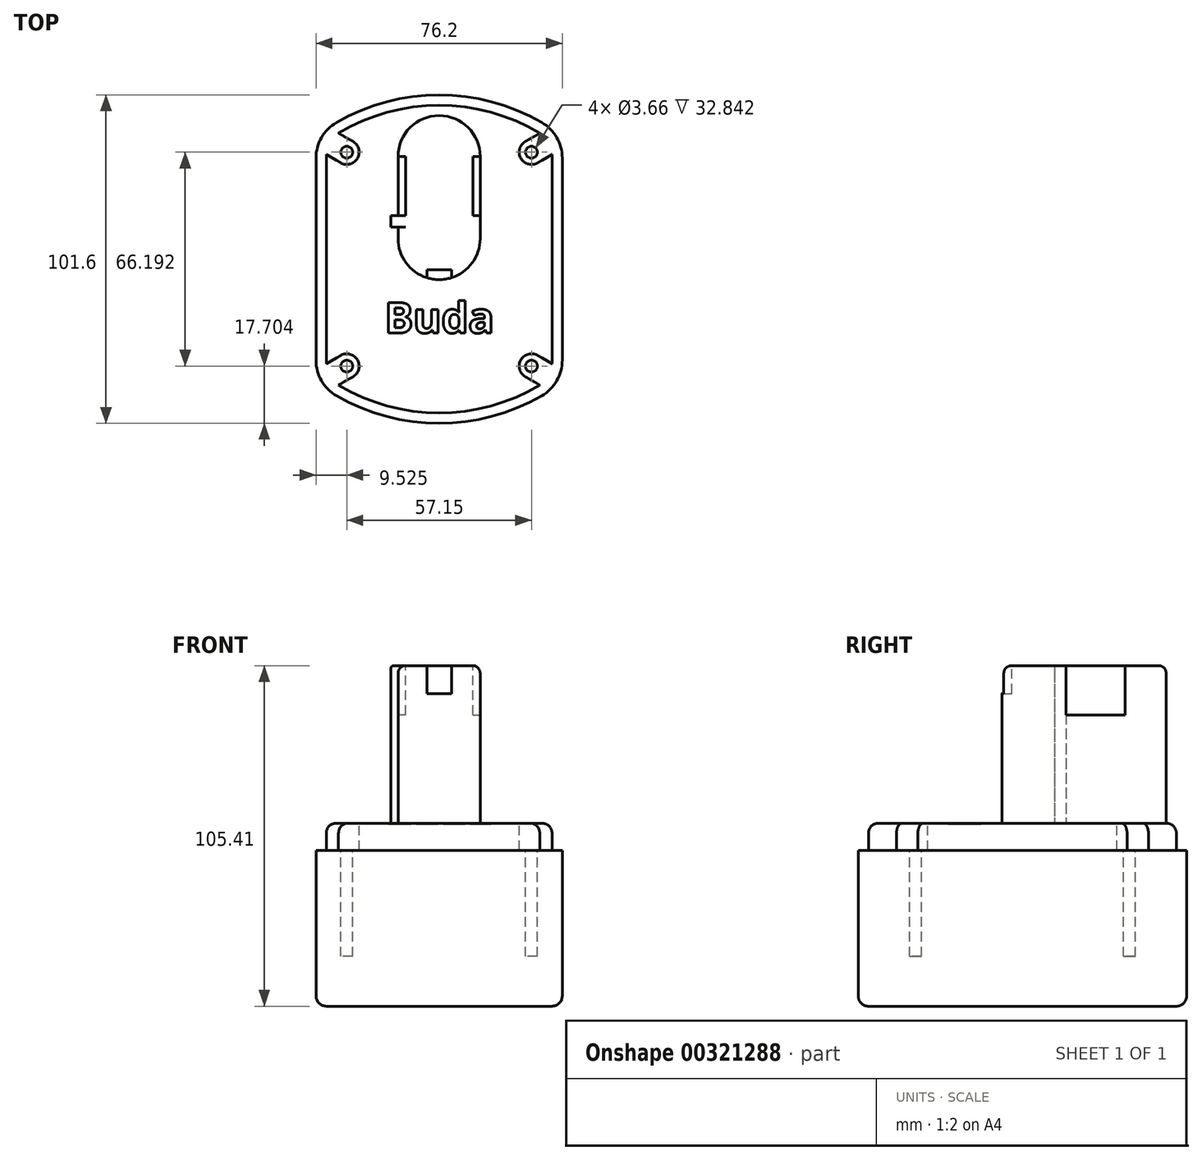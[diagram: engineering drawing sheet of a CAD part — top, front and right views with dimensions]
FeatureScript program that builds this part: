
annotation { "Feature Type Name" : "Feature", "Feature Type Description" : "" }
export const myFeature = defineFeature(function(context is Context, id is Id, definition is map)
    precondition{}
    {
        {
            var Q0;
            Q0=qCreatedBy(makeId("Top.planeOp"),FACE);
            var sketch = newSketch(context, id + "F0", { "sketchPlane" : qUnion([Q0])});
            skLineSegment(sketch, "E0.bottom", {"start": v(38.1, 38.1) * mm, "end": v(-38.1, 38.1) * mm, "construction": true});
            skLineSegment(sketch, "E0.top", {"start": v(38.1, -38.1) * mm, "end": v(-38.1, -38.1) * mm, "construction": true});
            skLineSegment(sketch, "E0.left", {"start": v(38.1, 38.1) * mm, "end": v(38.1, -38.1) * mm});
            skLineSegment(sketch, "E0.right", {"start": v(-38.1, 38.1) * mm, "end": v(-38.1, -38.1) * mm});
            skPoint(sketch, "E0.middle", {"position": v(0, 0) * mm});
            skLineSegment(sketch, "E1", {"start": v(0, 38.1) * mm, "end": v(0, 50.8) * mm, "construction": true});
            skPoint(sketch, "E1.endSnap0", {"position": v(0, 38.1) * mm});
            skArc(sketch, "E2", {"start": v(38.1, 38.1) * mm, "mid": v(0, 50.8) * mm, "end": v(-38.1, 38.1) * mm});
            skLineSegment(sketch, "E3", {"start": v(-38.1, 0) * mm, "end": v(38.1, 0) * mm, "construction": true});
            skArc(sketch, "E4.MirrorCS", {"start": v(38.1, -38.1) * mm, "mid": v(0, -50.8) * mm, "end": v(-38.1, -38.1) * mm});
            skSolve(sketch);
        }
        {
            var Q0;
            Q0 = qSketchRegion(id + "F0", true);
            extrude(context, id + "F1", {"entities" : qUnion([Q0]), "oppositeDirection" : true, "depth" : 48.26 * mm});
        }
        {
            var Q0;
            Q0=makeQuery(id+"F1.opExtrude","CAP_FACE",FACE,{"disambiguationData":[OSD([sQuery(id+"F0.wireOp",EDGE,"E0.left"),sQuery(id+"F0.wireOp",EDGE,"E0.right"),sQuery(id+"F0.wireOp",EDGE,"E2"),sQuery(id+"F0.wireOp",EDGE,"E4.MirrorCS")])],"isStart":true});
            var sketch = newSketch(context, id + "F2", { "sketchPlane" : qUnion([Q0])});
            skArc(sketch, "E5.0.0", {"start": v(38.1, 38.1) * mm, "mid": v(0, 50.8) * mm, "end": v(-38.1, 38.1) * mm, "construction": true});
            skLineSegment(sketch, "E5.0.1", {"start": v(-38.1, 38.1) * mm, "end": v(-38.1, -38.1) * mm, "construction": true});
            skArc(sketch, "E5.0.2", {"start": v(-38.1, -38.1) * mm, "mid": v(0, -50.8) * mm, "end": v(38.1, -38.1) * mm, "construction": true});
            skLineSegment(sketch, "E5.0.3", {"start": v(38.1, -38.1) * mm, "end": v(38.1, 38.1) * mm, "construction": true});
            skArc(sketch, "E6.0", {"start": v(34.93, 36.49) * mm, "mid": v(0, 47.62) * mm, "end": v(-34.92, 36.49) * mm});
            skLineSegment(sketch, "E6.1", {"start": v(34.93, -36.49) * mm, "end": v(34.93, 36.49) * mm});
            skArc(sketch, "E6.2", {"start": v(-34.93, -36.49) * mm, "mid": v(0, -47.62) * mm, "end": v(34.93, -36.49) * mm});
            skLineSegment(sketch, "E6.3", {"start": v(-34.93, 36.49) * mm, "end": v(-34.93, -36.49) * mm});
            skSolve(sketch);
        }
        {
            var Q0;
            Q0 = qSketchRegion(id + "F2", true);
            extrude(context, id + "F3", {"entities" : qUnion([Q0]), "operationType" : NewBodyOperationType.ADD, "depth" : 8.38 * mm});
        }
        {
            var Q0;
            Q0=makeQuery(id+"F3.opExtrude","CAP_FACE",FACE,{"disambiguationData":[OSD([sQuery(id+"F2.wireOp",EDGE,"E6.0"),sQuery(id+"F2.wireOp",EDGE,"E6.1"),sQuery(id+"F2.wireOp",EDGE,"E6.2"),sQuery(id+"F2.wireOp",EDGE,"E6.3")])],"isStart":false});
            var sketch = newSketch(context, id + "F4", { "sketchPlane" : qUnion([Q0])});
            skLineSegment(sketch, "E7.bottom", {"start": v(28.58, 33.1) * mm, "end": v(-28.57, 33.1) * mm, "construction": true});
            skLineSegment(sketch, "E7.top", {"start": v(28.57, -33.1) * mm, "end": v(-28.58, -33.1) * mm, "construction": true});
            skLineSegment(sketch, "E7.left", {"start": v(28.58, 33.1) * mm, "end": v(28.57, -33.1) * mm, "construction": true});
            skLineSegment(sketch, "E7.right", {"start": v(-28.57, 33.1) * mm, "end": v(-28.58, -33.1) * mm, "construction": true});
            skPoint(sketch, "E7.middle", {"position": v(0, 0) * mm});
            skLineSegment(sketch, "E8", {"start": v(-28.58, -33.1) * mm, "end": v(-50.57, -45.8) * mm, "construction": true});
            skArc(sketch, "E9.0.startCap", {"start": v(-30.48, -29.8) * mm, "mid": v(-25.28, -31.2) * mm, "end": v(-26.67, -36.4) * mm});
            skArc(sketch, "E9.0.endCap", {"start": v(-48.67, -49.1) * mm, "mid": v(-53.87, -47.7) * mm, "end": v(-52.48, -42.5) * mm});
            skLineSegment(sketch, "E9.0.left", {"start": v(-26.67, -36.4) * mm, "end": v(-48.67, -49.1) * mm});
            skLineSegment(sketch, "E9.0.right", {"start": v(-30.48, -29.8) * mm, "end": v(-52.48, -42.5) * mm});
            skLineSegment(sketch, "E10", {"start": v(-28.58, 0) * mm, "end": v(28.58, 0) * mm, "construction": true});
            skLineSegment(sketch, "E11", {"start": v(0, 33.1) * mm, "end": v(0, -33.1) * mm, "construction": true});
            skArc(sketch, "E12.MirrorCS", {"start": v(30.48, -29.8) * mm, "mid": v(25.28, -31.2) * mm, "end": v(26.67, -36.4) * mm});
            skLineSegment(sketch, "E13.MirrorCS", {"start": v(30.48, -29.8) * mm, "end": v(52.48, -42.5) * mm});
            skLineSegment(sketch, "E14.MirrorCS", {"start": v(26.67, -36.4) * mm, "end": v(48.67, -49.1) * mm});
            skArc(sketch, "E15.MirrorCS", {"start": v(48.67, -49.1) * mm, "mid": v(53.87, -47.7) * mm, "end": v(52.48, -42.5) * mm});
            skArc(sketch, "E16.MirrorCS", {"start": v(-30.48, 29.8) * mm, "mid": v(-25.28, 31.2) * mm, "end": v(-26.67, 36.4) * mm});
            skLineSegment(sketch, "E17.MirrorCS", {"start": v(-30.48, 29.8) * mm, "end": v(-52.48, 42.5) * mm});
            skLineSegment(sketch, "E18.MirrorCS", {"start": v(-26.67, 36.4) * mm, "end": v(-48.67, 49.1) * mm});
            skArc(sketch, "E19.MirrorCS", {"start": v(-48.67, 49.1) * mm, "mid": v(-53.87, 47.7) * mm, "end": v(-52.48, 42.5) * mm});
            skArc(sketch, "E20.MirrorCS", {"start": v(30.48, 29.8) * mm, "mid": v(25.28, 31.2) * mm, "end": v(26.67, 36.4) * mm});
            skLineSegment(sketch, "E21.MirrorCS", {"start": v(30.48, 29.8) * mm, "end": v(52.48, 42.5) * mm});
            skLineSegment(sketch, "E22.MirrorCS", {"start": v(26.67, 36.4) * mm, "end": v(48.67, 49.1) * mm});
            skArc(sketch, "E23.MirrorCS", {"start": v(48.67, 49.1) * mm, "mid": v(53.87, 47.7) * mm, "end": v(52.48, 42.5) * mm});
            skCircle(sketch, "E24", {"center": v(-28.57, 33.1) * mm, "radius": 1.83 * mm, "construction": true});
            skCircle(sketch, "E25", {"center": v(28.58, 33.1) * mm, "radius": 1.83 * mm, "construction": true});
            skCircle(sketch, "E26", {"center": v(-28.58, -33.1) * mm, "radius": 1.83 * mm, "construction": true});
            skCircle(sketch, "E27", {"center": v(28.57, -33.1) * mm, "radius": 1.83 * mm, "construction": true});
            skSolve(sketch);
        }
        {
            var Q0;
            Q0 = qSketchRegion(id + "F4", true);
            var Q1;
            Q1=makeQuery(id+"F1.opExtrude","CAP_FACE",FACE,{"disambiguationData":[OSD([sQuery(id+"F0.wireOp",EDGE,"E0.left"),sQuery(id+"F0.wireOp",EDGE,"E0.right"),sQuery(id+"F0.wireOp",EDGE,"E2"),sQuery(id+"F0.wireOp",EDGE,"E4.MirrorCS")])],"isStart":true});
            extrude(context, id + "F5", {"entities" : qUnion([Q0]), "operationType" : NewBodyOperationType.REMOVE, "endBound" : BoundingType.UP_TO_SURFACE, "oppositeDirection" : true, "endBoundEntityFace" : qUnion([Q1]), "depth" : 25.4 * mm});
        }
        {
            var Q0;
            Q0=makeQuery(id+"F5.boolean.opBoolean","MERGE",FACE,{"derivedFrom":[makeQuery(id+"F1.opExtrude","CAP_FACE",FACE,{"disambiguationData":[OSD([sQuery(id+"F0.wireOp",EDGE,"E0.left"),sQuery(id+"F0.wireOp",EDGE,"E0.right"),sQuery(id+"F0.wireOp",EDGE,"E2"),sQuery(id+"F0.wireOp",EDGE,"E4.MirrorCS")])],"isStart":true})],"fromTools":[makeQuery(id+"F5.opExtrude","CAP_FACE",FACE,{"disambiguationData":[OSD([sQuery(id+"F4.wireOp",EDGE,"E9.0.startCap"),sQuery(id+"F4.wireOp",EDGE,"E9.0.endCap"),sQuery(id+"F4.wireOp",EDGE,"E9.0.left"),sQuery(id+"F4.wireOp",EDGE,"E9.0.right")])],"isStart":false}),makeQuery(id+"F5.opExtrude","CAP_FACE",FACE,{"disambiguationData":[OSD([sQuery(id+"F4.wireOp",EDGE,"E12.MirrorCS"),sQuery(id+"F4.wireOp",EDGE,"E13.MirrorCS"),sQuery(id+"F4.wireOp",EDGE,"E14.MirrorCS"),sQuery(id+"F4.wireOp",EDGE,"E15.MirrorCS")])],"isStart":false}),makeQuery(id+"F5.opExtrude","CAP_FACE",FACE,{"disambiguationData":[OSD([sQuery(id+"F4.wireOp",EDGE,"E16.MirrorCS"),sQuery(id+"F4.wireOp",EDGE,"E17.MirrorCS"),sQuery(id+"F4.wireOp",EDGE,"E18.MirrorCS"),sQuery(id+"F4.wireOp",EDGE,"E19.MirrorCS")])],"isStart":false}),makeQuery(id+"F5.opExtrude","CAP_FACE",FACE,{"disambiguationData":[OSD([sQuery(id+"F4.wireOp",EDGE,"E20.MirrorCS"),sQuery(id+"F4.wireOp",EDGE,"E21.MirrorCS"),sQuery(id+"F4.wireOp",EDGE,"E22.MirrorCS"),sQuery(id+"F4.wireOp",EDGE,"E23.MirrorCS")])],"isStart":false})]});
            var sketch = newSketch(context, id + "F6", { "sketchPlane" : qUnion([Q0])});
            skCircle(sketch, "E28.0", {"center": v(28.57, -33.1) * mm, "radius": 1.83 * mm});
            skCircle(sketch, "E28.1", {"center": v(28.58, 33.1) * mm, "radius": 1.83 * mm});
            skCircle(sketch, "E28.2", {"center": v(-28.57, 33.1) * mm, "radius": 1.83 * mm});
            skCircle(sketch, "E28.3", {"center": v(-28.58, -33.1) * mm, "radius": 1.83 * mm});
            skSolve(sketch);
        }
        {
            var Q0;
            Q0 = qSketchRegion(id + "F6", true);
            extrude(context, id + "F7", {"entities" : qUnion([Q0]), "operationType" : NewBodyOperationType.REMOVE, "oppositeDirection" : true, "depth" : 32.84 * mm});
        }
        {
            var Q0;
            Q0=qCreatedBy(makeId("Top.planeOp"),FACE);
            var sketch = newSketch(context, id + "F8", { "sketchPlane" : qUnion([Q0])});
            skLineSegment(sketch, "E29", {"start": v(0, 6.35) * mm, "end": v(0, 31.75) * mm, "construction": true});
            skArc(sketch, "E30.0.startCap", {"start": v(12.7, 6.35) * mm, "mid": v(0, -6.35) * mm, "end": v(-12.7, 6.35) * mm});
            skArc(sketch, "E30.0.endCap", {"start": v(-12.7, 31.75) * mm, "mid": v(0, 44.45) * mm, "end": v(12.7, 31.75) * mm});
            skLineSegment(sketch, "E30.0.left", {"start": v(-12.7, 6.35) * mm, "end": v(-12.7, 31.75) * mm});
            skLineSegment(sketch, "E30.0.right", {"start": v(12.7, 6.35) * mm, "end": v(12.7, 31.75) * mm});
            skPoint(sketch, "E31", {"position": v(0, 19.05) * mm});
            skPoint(sketch, "E32", {"position": v(0, 44.45) * mm});
            skPoint(sketch, "E33", {"position": v(0, -6.35) * mm});
            skSolve(sketch);
        }
        {
            var Q0;
            Q0 = qSketchRegion(id + "F8", true);
            extrude(context, id + "F9", {"entities" : qUnion([Q0]), "operationType" : NewBodyOperationType.ADD, "depth" : 57.15 * mm});
        }
        {
            var Q0;
            Q0=makeQuery(id+"F3.opExtrude","CAP_FACE",FACE,{"disambiguationData":[OSD([sQuery(id+"F2.wireOp",EDGE,"E6.0"),sQuery(id+"F2.wireOp",EDGE,"E6.1"),sQuery(id+"F2.wireOp",EDGE,"E6.2"),sQuery(id+"F2.wireOp",EDGE,"E6.3")])],"isStart":false});
            var sketch = newSketch(context, id + "F10", { "sketchPlane" : qUnion([Q0])});
            skLineSegment(sketch, "E34.bottom", {"start": v(-12.7, 13.46) * mm, "end": v(-14.99, 13.46) * mm});
            skLineSegment(sketch, "E34.top", {"start": v(-12.7, 9.9) * mm, "end": v(-14.99, 9.9) * mm});
            skLineSegment(sketch, "E34.left", {"start": v(-12.7, 13.46) * mm, "end": v(-12.7, 9.9) * mm});
            skLineSegment(sketch, "E34.right", {"start": v(-14.99, 13.46) * mm, "end": v(-14.99, 9.9) * mm});
            skSolve(sketch);
        }
        {
            var Q0;
            Q0 = qSketchRegion(id + "F10", true);
            var Q1;
            Q1=makeQuery(id+"F9.opExtrude","CAP_FACE",FACE,{"disambiguationData":[OSD([sQuery(id+"F8.wireOp",EDGE,"E30.0.startCap"),sQuery(id+"F8.wireOp",EDGE,"E30.0.endCap"),sQuery(id+"F8.wireOp",EDGE,"E30.0.left"),sQuery(id+"F8.wireOp",EDGE,"E30.0.right")])],"isStart":false});
            extrude(context, id + "F11", {"entities" : qUnion([Q0]), "operationType" : NewBodyOperationType.ADD, "endBound" : BoundingType.UP_TO_SURFACE, "endBoundEntityFace" : qUnion([Q1]), "depth" : 25.4 * mm});
        }
        {
            var Q0;
            Q0=makeQuery(id+"F9.opExtrude","CAP_EDGE",EDGE,{"disambiguationData":[OSD([sQuery(id+"F8.wireOp",EDGE,"E30.0.right")])],"isStart":false});
            fillet(context, id + "F12", {"entities" : qUnion([Q0]), "radius" : 2.3 * mm, "tangentPropagation" : true, "allowEdgeOverflow" : false});
        }
        {
            var Q0;
            Q0=makeQuery(id+"F11.boolean.opBoolean","MERGE",FACE,{"derivedFrom":[makeQuery(id+"F9.opExtrude","CAP_FACE",FACE,{"disambiguationData":[OSD([sQuery(id+"F8.wireOp",EDGE,"E30.0.startCap"),sQuery(id+"F8.wireOp",EDGE,"E30.0.endCap"),sQuery(id+"F8.wireOp",EDGE,"E30.0.left"),sQuery(id+"F8.wireOp",EDGE,"E30.0.right")])],"isStart":false}),makeQuery(id+"F11.opExtrude","CAP_FACE",FACE,{"disambiguationData":[OSD([sQuery(id+"F10.wireOp",EDGE,"E34.bottom"),sQuery(id+"F10.wireOp",EDGE,"E34.top"),sQuery(id+"F10.wireOp",EDGE,"E34.left"),sQuery(id+"F10.wireOp",EDGE,"E34.right")])],"isStart":false})]});
            var sketch = newSketch(context, id + "F13", { "sketchPlane" : qUnion([Q0])});
            skLineSegment(sketch, "E35.bottom", {"start": v(10.41, 31.75) * mm, "end": v(12.7, 31.75) * mm});
            skLineSegment(sketch, "E35.top", {"start": v(10.41, 13.46) * mm, "end": v(12.7, 13.46) * mm});
            skLineSegment(sketch, "E35.left", {"start": v(10.41, 31.75) * mm, "end": v(10.41, 13.46) * mm});
            skLineSegment(sketch, "E35.right", {"start": v(12.7, 31.75) * mm, "end": v(12.7, 13.46) * mm});
            skLineSegment(sketch, "E36.0", {"start": v(0, 6.35) * mm, "end": v(0, 31.75) * mm, "construction": true});
            skLineSegment(sketch, "E37.MirrorCS", {"start": v(-10.41, 31.75) * mm, "end": v(-10.41, 13.46) * mm});
            skLineSegment(sketch, "E38.MirrorCS", {"start": v(-10.41, 31.75) * mm, "end": v(-12.7, 31.75) * mm});
            skLineSegment(sketch, "E39.MirrorCS", {"start": v(-12.7, 31.75) * mm, "end": v(-12.7, 13.46) * mm});
            skArc(sketch, "E40.0", {"start": v(12.7, 6.35) * mm, "mid": v(0, -6.35) * mm, "end": v(-12.7, 6.35) * mm});
            skArc(sketch, "E40.1", {"start": v(-10.41, 6.35) * mm, "mid": v(0, -4.06) * mm, "end": v(10.41, 6.35) * mm, "construction": true});
            skLineSegment(sketch, "E41", {"start": v(-3.81, -5.77) * mm, "end": v(-3.81, -3.34) * mm, "construction": true});
            skLineSegment(sketch, "E42", {"start": v(-3.8, -3.34) * mm, "end": v(3.81, -3.34) * mm, "construction": true});
            skLineSegment(sketch, "E43", {"start": v(3.81, -3.34) * mm, "end": v(3.81, -5.77) * mm, "construction": true});
            skSolve(sketch);
        }
        {
            var Q0;
            Q0 = qSketchRegion(id + "F13", true);
            var Q1;
            {var subQ0=sQuery(id+"F13.wireOp",EDGE,"E37.MirrorCS");Q1=makeQuery(id+"F13.imprint","IMPRINT",FACE,{"disambiguationData":[TD([[makeQuery(id+"F13.imprint","IMPRINT",EDGE,{"derivedFrom":subQ0}),-1.0]])]});}
            extrude(context, id + "F14", {"entities" : qUnion([Q0, Q1]), "operationType" : NewBodyOperationType.REMOVE, "oppositeDirection" : true, "depth" : 15.24 * mm});
        }
        {
            var Q0;
            {var subQ10=sQuery(id+"F13.wireOp",EDGE,"E35.left");Q0=makeQuery(id+"F13.imprint","IMPRINT",FACE,{"disambiguationData":[TD([[makeQuery(id+"F13.imprint","IMPRINT",EDGE,{"derivedFrom":subQ10}),1.0]])]});}
            var sketch = newSketch(context, id + "F15", { "sketchPlane" : qUnion([Q0])});
            skLineSegment(sketch, "E44.0", {"start": v(-3.81, -5.77) * mm, "end": v(-3.81, -3.34) * mm});
            skLineSegment(sketch, "E44.1", {"start": v(-3.8, -3.34) * mm, "end": v(3.81, -3.34) * mm});
            skLineSegment(sketch, "E44.2", {"start": v(3.81, -3.34) * mm, "end": v(3.81, -5.77) * mm});
            skArc(sketch, "E44.3", {"start": v(3.8, -5.77) * mm, "mid": v(0, -6.35) * mm, "end": v(-3.8, -5.77) * mm});
            skPoint(sketch, "E45.orphan", {"position": v(12.7, 6.35) * mm});
            skPoint(sketch, "E46.orphan", {"position": v(-12.7, 6.35) * mm});
            skSolve(sketch);
        }
        {
            var Q0;
            Q0 = qSketchRegion(id + "F15", true);
            extrude(context, id + "F16", {"entities" : qUnion([Q0]), "operationType" : NewBodyOperationType.REMOVE, "oppositeDirection" : true, "depth" : 8.64 * mm});
        }
        {
            var Q0;
            Q0=makeQuery(id+"F11.opExtrude","CAP_EDGE",EDGE,{"disambiguationData":[OSD([sQuery(id+"F10.wireOp",EDGE,"E34.right")])],"isStart":false});
            fillet(context, id + "F17", {"entities" : qUnion([Q0]), "radius" : 1.02 * mm, "tangentPropagation" : true, "allowEdgeOverflow" : false});
        }
        {
            var Q0;
            Q0=makeQuery(id+"F3.opExtrude","CAP_FACE",FACE,{"disambiguationData":[OSD([sQuery(id+"F2.wireOp",EDGE,"E6.0"),sQuery(id+"F2.wireOp",EDGE,"E6.1"),sQuery(id+"F2.wireOp",EDGE,"E6.2"),sQuery(id+"F2.wireOp",EDGE,"E6.3")])],"isStart":false});
            var sketch = newSketch(context, id + "F18", { "sketchPlane" : qUnion([Q0])});
            skText(sketch, "E47", { "text": "Buda", "fontName": "OpenSans-Bold.ttf"});
            skArc(sketch, "E48.0", {"start": v(38.1, -38.1) * mm, "mid": v(0, -50.8) * mm, "end": v(-38.1, -38.1) * mm, "construction": true});
            skLineSegment(sketch, "E49", {"start": v(0, -47.62) * mm, "end": v(0, -22.86) * mm, "construction": true});
            const initialGuessF18  = {"E47": [-0.0169, -0.02286, 1, 0, 0.00952]};
            skSetInitialGuess(sketch, initialGuessF18);
            skSolve(sketch);
        }
        {
            var Q0;
            Q0 = qSketchRegion(id + "F18", true);
            extrude(context, id + "F19", {"entities" : qUnion([Q0]), "operationType" : NewBodyOperationType.REMOVE, "oppositeDirection" : true, "depth" : 0.25 * mm});
        }
        {
            var Q0;
            Q0=makeQuery(id+"F1.opExtrude","SWEPT_EDGE",EDGE,{"disambiguationData":[OSD([sQuery(id+"F0.wireOp",EDGE,"E0.left"),sQuery(id+"F0.wireOp",EDGE,"E4.MirrorCS")])]});
            var Q1;
            Q1=makeQuery(id+"F1.opExtrude","SWEPT_EDGE",EDGE,{"disambiguationData":[OSD([sQuery(id+"F0.wireOp",EDGE,"E0.left"),sQuery(id+"F0.wireOp",EDGE,"E2")])]});
            var Q2;
            Q2=makeQuery(id+"F1.opExtrude","SWEPT_EDGE",EDGE,{"disambiguationData":[OSD([sQuery(id+"F0.wireOp",EDGE,"E0.right"),sQuery(id+"F0.wireOp",EDGE,"E4.MirrorCS")])]});
            var Q3;
            Q3=makeQuery(id+"F1.opExtrude","SWEPT_EDGE",EDGE,{"disambiguationData":[OSD([sQuery(id+"F0.wireOp",EDGE,"E0.right"),sQuery(id+"F0.wireOp",EDGE,"E2")])]});
            fillet(context, id + "F20", {"entities" : qUnion([Q0, Q1, Q2, Q3]), "radius" : 12.7 * mm, "tangentPropagation" : true, "allowEdgeOverflow" : false});
        }
        {
            var Q0;
            Q0=makeQuery(id+"F3.opExtrude","CAP_EDGE",EDGE,{"disambiguationData":[OSD([sQuery(id+"F2.wireOp",EDGE,"E6.2")])],"isStart":false});
            var Q1;
            Q1=makeQuery(id+"F3.opExtrude","CAP_EDGE",EDGE,{"disambiguationData":[OSD([sQuery(id+"F2.wireOp",EDGE,"E6.1")])],"isStart":false});
            var Q2;
            Q2=makeQuery(id+"F3.opExtrude","CAP_EDGE",EDGE,{"disambiguationData":[OSD([sQuery(id+"F2.wireOp",EDGE,"E6.3")])],"isStart":false});
            var Q3;
            Q3=makeQuery(id+"F3.opExtrude","CAP_EDGE",EDGE,{"disambiguationData":[OSD([sQuery(id+"F2.wireOp",EDGE,"E6.0")])],"isStart":false});
            fillet(context, id + "F21", {"entities" : qUnion([Q0, Q1, Q2, Q3]), "radius" : 3.05 * mm, "tangentPropagation" : true, "allowEdgeOverflow" : false});
        }
        {
            var Q0;
            Q0=makeQuery(id+"F1.opExtrude","CAP_EDGE",EDGE,{"disambiguationData":[OSD([sQuery(id+"F0.wireOp",EDGE,"E0.left")])],"isStart":false});
            fillet(context, id + "F22", {"entities" : qUnion([Q0]), "radius" : 3.17 * mm, "tangentPropagation" : true, "allowEdgeOverflow" : false});
        }
    });
